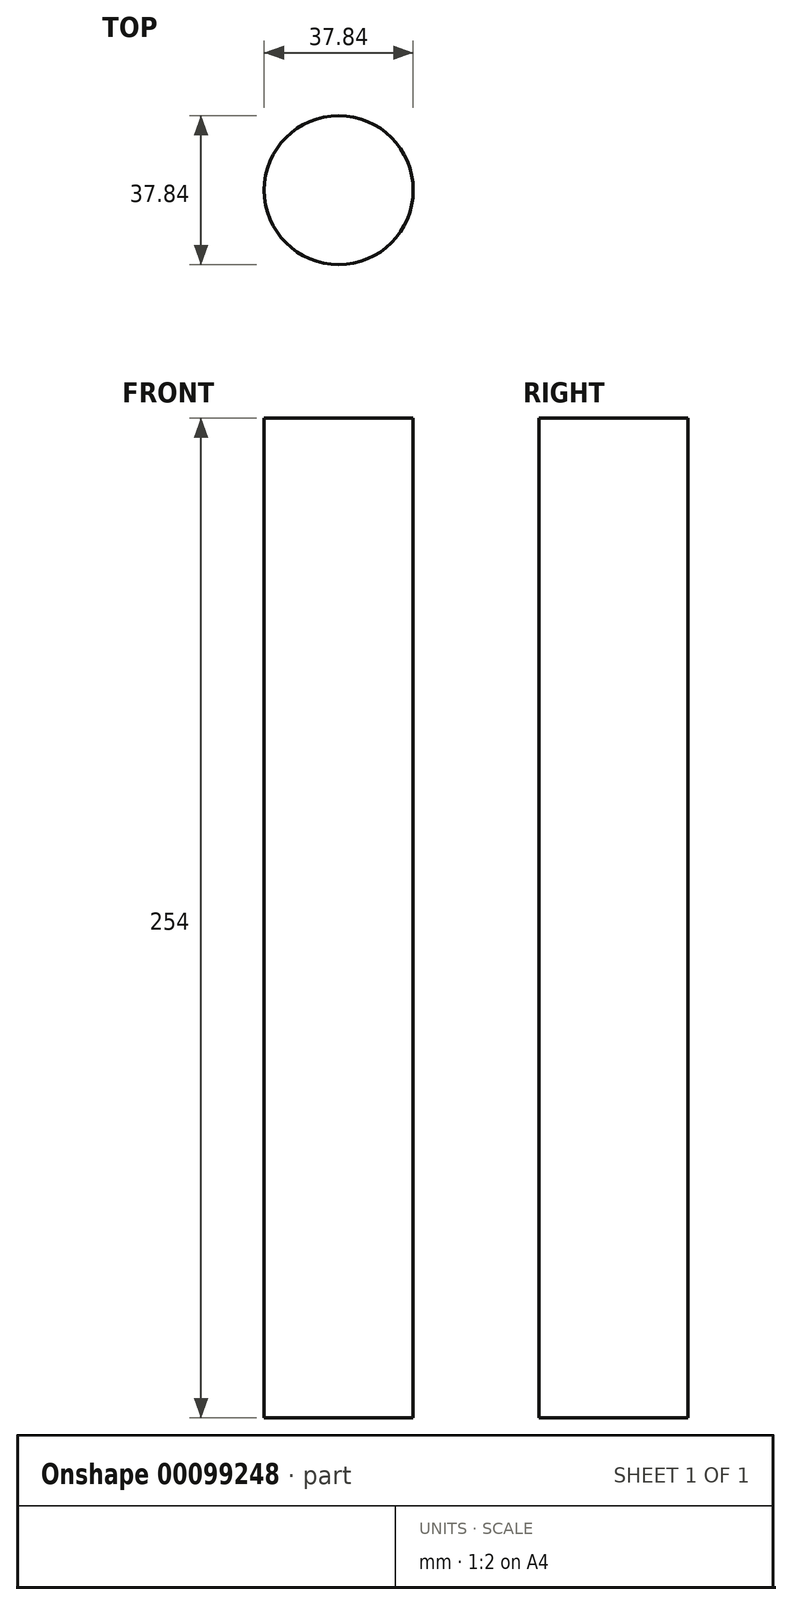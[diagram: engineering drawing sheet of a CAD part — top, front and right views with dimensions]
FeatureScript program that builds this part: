
annotation { "Feature Type Name" : "Feature", "Feature Type Description" : "" }
export const myFeature = defineFeature(function(context is Context, id is Id, definition is map)
    precondition{}
    {
        {
            var Q0;
            Q0=qCreatedBy(makeId("Top.planeOp"),FACE);
            var sketch = newSketch(context, id + "F0", { "sketchPlane" : qUnion([Q0])});
            skCircle(sketch, "E0", {"center": v(0, 0) * mm, "radius": 18.92 * mm});
            skSolve(sketch);
        }
        {
            var Q0;
            Q0=makeQuery(id+"F0.imprint","IMPRINT",FACE,{"disambiguationData":[TD([[makeQuery(id+"F0.imprint","IMPRINT",EDGE,{"derivedFrom":sQuery(id+"F0.wireOp",EDGE,"E0")}),1.0]])]});
            extrude(context, id + "F1", {"entities" : qUnion([Q0]), "endBound" : BoundingType.SYMMETRIC, "depth" : 254 * mm});
        }
    });
